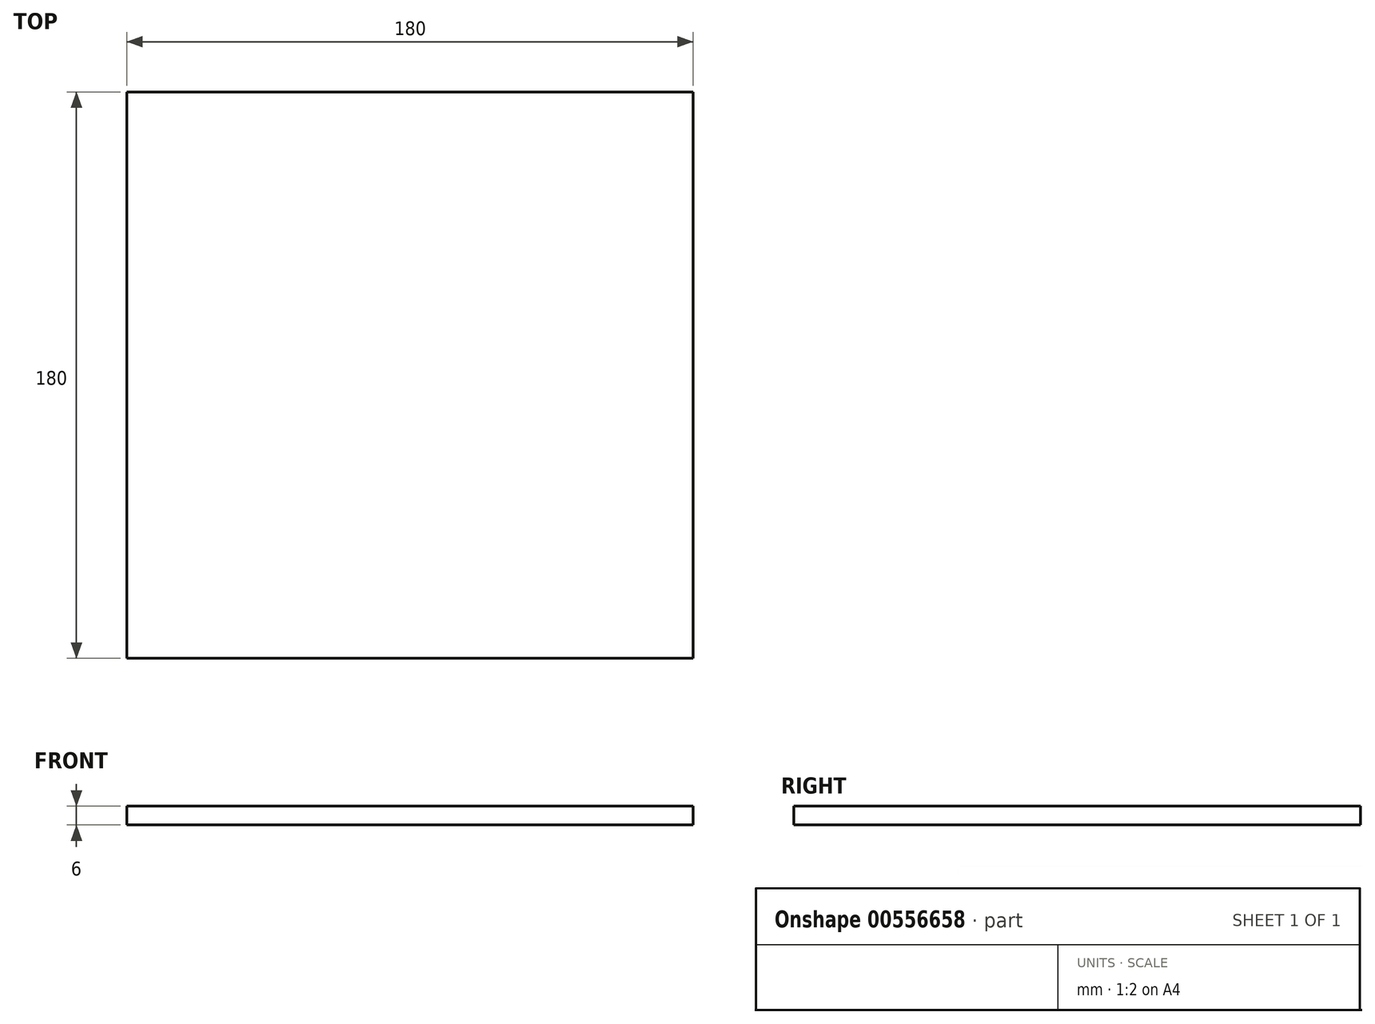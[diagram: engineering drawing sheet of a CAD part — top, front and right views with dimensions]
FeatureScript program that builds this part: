
annotation { "Feature Type Name" : "Feature", "Feature Type Description" : "" }
export const myFeature = defineFeature(function(context is Context, id is Id, definition is map)
    precondition{}
    {
        {
            var Q0;
            Q0=qCreatedBy(makeId("Top.planeOp"),FACE);
            var sketch = newSketch(context, id + "F0", { "sketchPlane" : qUnion([Q0])});
            skLineSegment(sketch, "E0", {"start": v(0, 0) * mm, "end": v(0, 180) * mm});
            skLineSegment(sketch, "E1", {"start": v(0, 180) * mm, "end": v(180, 180) * mm});
            skLineSegment(sketch, "E2", {"start": v(180, 180) * mm, "end": v(180, 0) * mm});
            skLineSegment(sketch, "E3", {"start": v(180, 0) * mm, "end": v(0, 0) * mm});
            skSolve(sketch);
        }
        {
            var Q0;
            Q0 = qSketchRegion(id + "F0", true);
            extrude(context, id + "F1", {"entities" : qUnion([Q0]), "depth" : 6 * mm, "offsetDistance" : 25 * mm});
        }
    });
